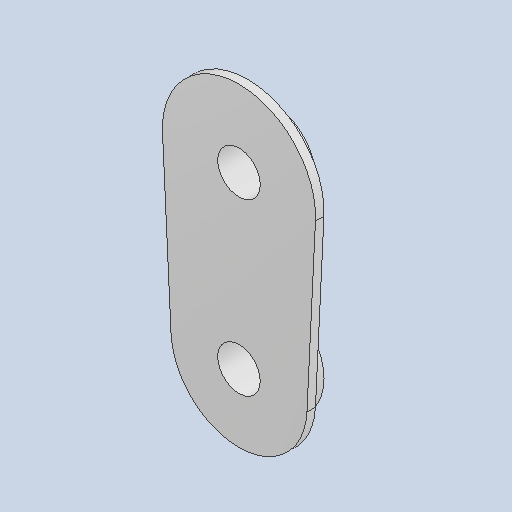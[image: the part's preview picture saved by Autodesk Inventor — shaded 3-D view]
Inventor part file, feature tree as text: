
AUTODESK INVENTOR PART (.ipt)
format: ipt  version: 2023 (Build 270158030, 158C)  size: 111,104 bytes
history: native  units: mm
features: other x3, sketch x1
ambient origin geometry x8: Origin, YZ Plane, XZ Plane, XY Plane, X Axis, Y Axis, Z Axis, Center Point
bodies: Solid1 (feature_tree)
feature tree (4):
  other  "ヘッケン抑え.ipt"
  other  "Solid1::ヘッケン抑え.ipt"
  other  "TaggingFeature1"
  sketch  "Sketch1"  dims[d0=10.0mm]
